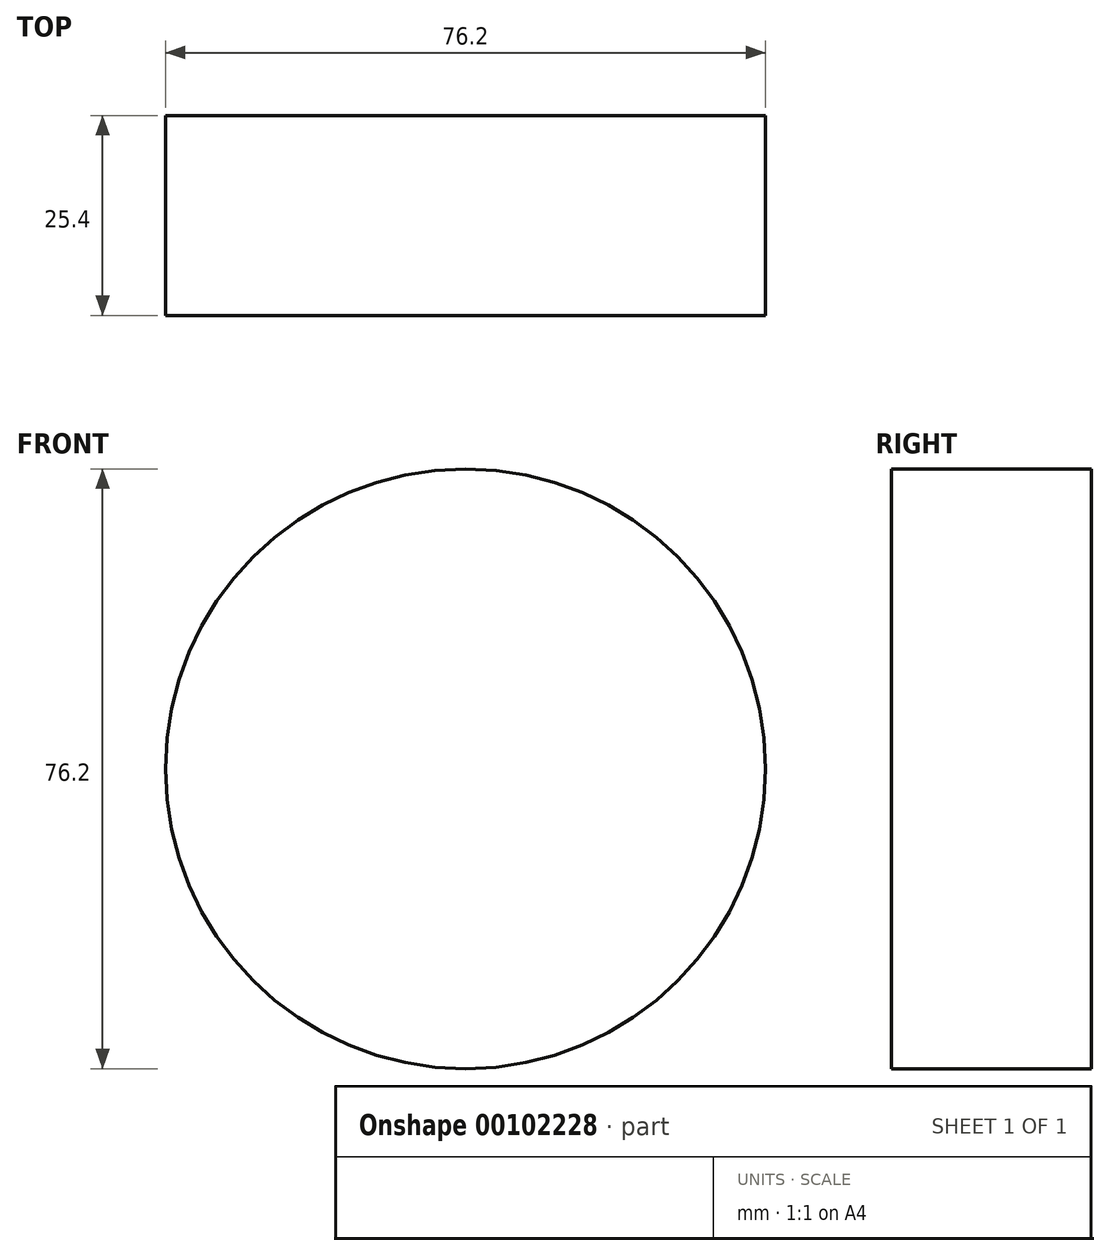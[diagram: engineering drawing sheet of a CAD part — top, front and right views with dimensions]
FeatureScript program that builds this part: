
annotation { "Feature Type Name" : "Feature", "Feature Type Description" : "" }
export const myFeature = defineFeature(function(context is Context, id is Id, definition is map)
    precondition{}
    {
        {
            var Q0;
            Q0=qCreatedBy(makeId("Front.planeOp"),FACE);
            var sketch = newSketch(context, id + "F0", { "sketchPlane" : qUnion([Q0])});
            skCircle(sketch, "E0", {"center": v(0, 0) * mm, "radius": 38.1 * mm});
            skSolve(sketch);
        }
        {
            var Q0;
            Q0=makeQuery(id+"F0.imprint","IMPRINT",FACE,{"disambiguationData":[TD([[makeQuery(id+"F0.imprint","IMPRINT",EDGE,{"derivedFrom":sQuery(id+"F0.wireOp",EDGE,"E0")}),1.0]])]});
            extrude(context, id + "F1", {"entities" : qUnion([Q0]), "depth" : 25.4 * mm});
        }
    });
